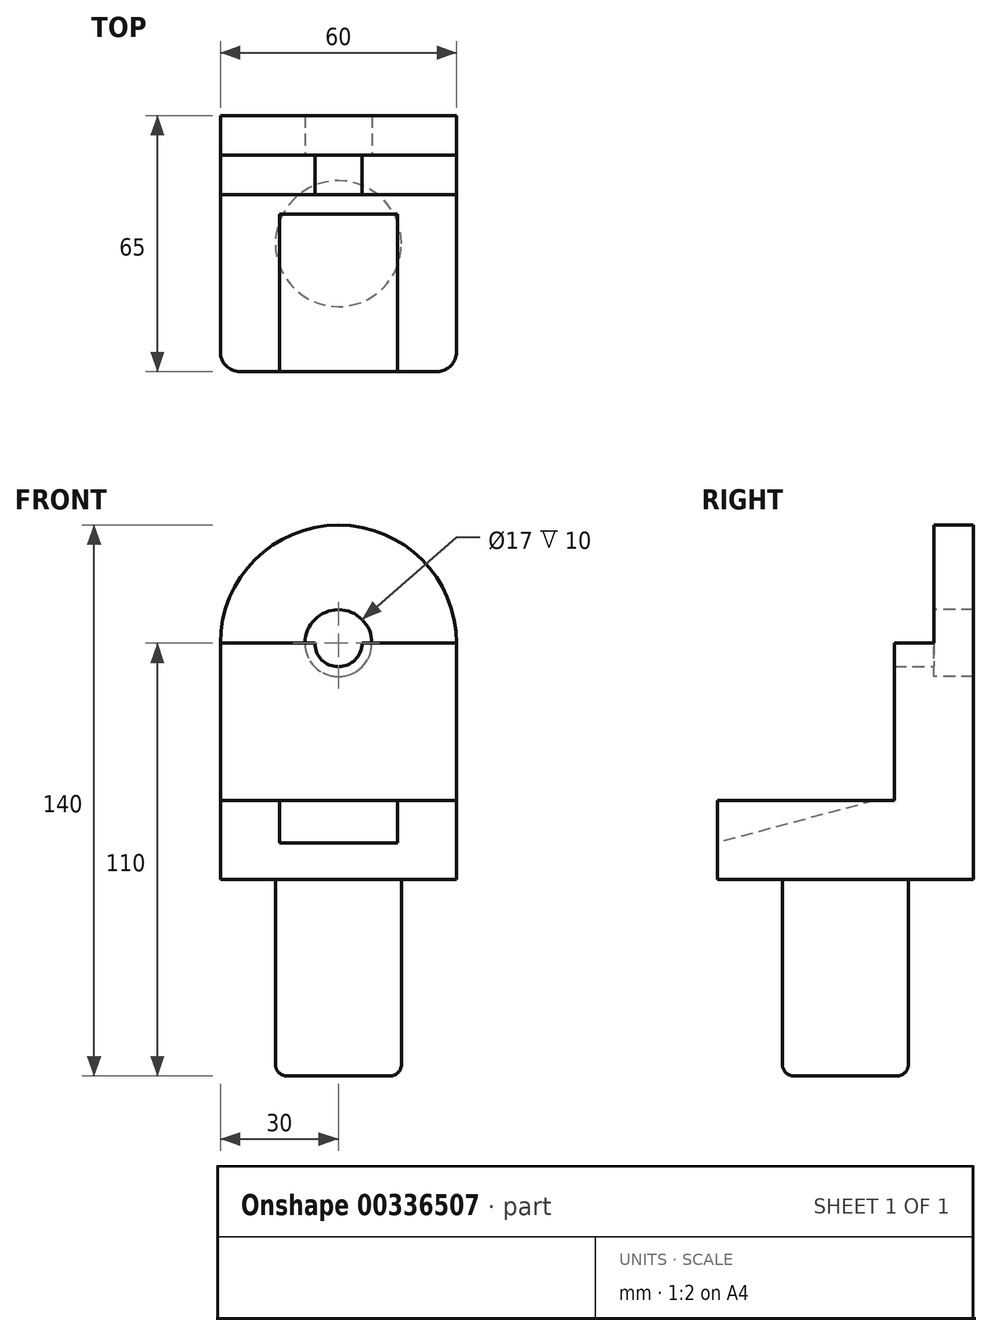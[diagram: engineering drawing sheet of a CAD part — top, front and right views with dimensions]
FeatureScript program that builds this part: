
annotation { "Feature Type Name" : "Feature", "Feature Type Description" : "" }
export const myFeature = defineFeature(function(context is Context, id is Id, definition is map)
    precondition{}
    {
        {
            var Q0;
            Q0=qCreatedBy(makeId("Top.planeOp"),FACE);
            var sketch = newSketch(context, id + "F0", { "sketchPlane" : qUnion([Q0])});
            skCircle(sketch, "E0", {"center": v(0, 0) * mm, "radius": 16 * mm});
            skSolve(sketch);
        }
        {
            var Q0;
            Q0=makeQuery(id+"F0.imprint","IMPRINT",FACE,{"disambiguationData":[TD([[makeQuery(id+"F0.imprint","IMPRINT",EDGE,{"derivedFrom":sQuery(id+"F0.wireOp",EDGE,"E0")}),1.0]])]});
            extrude(context, id + "F1", {"entities" : qUnion([Q0]), "depth" : 50 * mm});
        }
        {
            var Q0;
            Q0=makeQuery(id+"F1.opExtrude","CAP_FACE",FACE,{"disambiguationData":[OSD([sQuery(id+"F0.wireOp",EDGE,"E0")])],"isStart":false});
            var sketch = newSketch(context, id + "F2", { "sketchPlane" : qUnion([Q0])});
            skLineSegment(sketch, "E1", {"start": v(-30, 0) * mm, "end": v(-30, 32.5) * mm});
            skLineSegment(sketch, "E2", {"start": v(0, 32.5) * mm, "end": v(-30, 32.5) * mm});
            skLineSegment(sketch, "E3", {"start": v(30, 0) * mm, "end": v(30, -32.5) * mm});
            skLineSegment(sketch, "E4", {"start": v(0, -32.5) * mm, "end": v(30, -32.5) * mm});
            skLineSegment(sketch, "E5", {"start": v(0, -32.5) * mm, "end": v(-30, -32.5) * mm});
            skLineSegment(sketch, "E6", {"start": v(-30, -32.5) * mm, "end": v(-30, 0) * mm});
            skLineSegment(sketch, "E7", {"start": v(30, 0) * mm, "end": v(30, 32.5) * mm});
            skLineSegment(sketch, "E8", {"start": v(30, 32.5) * mm, "end": v(0, 32.5) * mm});
            skPoint(sketch, "E9.start.orphan", {"position": v(0, 0) * mm});
            skLineSegment(sketch, "E10", {"start": v(-30, 32.5) * mm, "end": v(-30, 7.5) * mm});
            skLineSegment(sketch, "E11", {"start": v(-30, 7.5) * mm, "end": v(30, 7.5) * mm});
            skLineSegment(sketch, "E12", {"start": v(30, -32.5) * mm, "end": v(15, -32.5) * mm});
            skLineSegment(sketch, "E13", {"start": v(30, 7.5) * mm, "end": v(15, 7.5) * mm});
            skLineSegment(sketch, "E14", {"start": v(15, 7.5) * mm, "end": v(15, -32.5) * mm});
            skSolve(sketch);
        }
        {
            var Q0;
            Q0=makeQuery(id+"F2.imprint","IMPRINT",FACE,{"disambiguationData":[TD([[makeQuery(id+"F2.imprint","IMPRINT",EDGE,{"derivedFrom":sQuery(id+"F2.wireOp",EDGE,"E2")}),1.0]])]});
            var Q1;
            {var subQ0=sQuery(id+"F2.wireOp",EDGE,"E11");var subQ1=makeQuery(id+"F1.opExtrude","CAP_EDGE",EDGE,{"disambiguationData":[OSD([sQuery(id+"F0.wireOp",EDGE,"E0")])],"isStart":false});var subQ2=makeQuery(id+"F2.imprint","INTERSECT",VERTEX,{"disambiguationData":[OD(0.0)],"derivedFrom":[subQ1,subQ0]});Q1=makeQuery(id+"F2.imprint","IMPRINT",FACE,{"disambiguationData":[TD([[makeQuery(id+"F2.imprint","IMPRINT",EDGE,{"disambiguationData":[TD([[subQ2,-1.0]])],"derivedFrom":subQ0}),1.0]])]});}
            extrude(context, id + "F3", {"entities" : qUnion([Q0, Q1]), "operationType" : NewBodyOperationType.ADD, "depth" : 20 * mm});
        }
        {
            var Q0;
            {var subQ0=sQuery(id+"F2.wireOp",EDGE,"E14");var subQ1=makeQuery(id+"F1.opExtrude","CAP_EDGE",EDGE,{"disambiguationData":[OSD([sQuery(id+"F0.wireOp",EDGE,"E0")])],"isStart":false});var subQ2=makeQuery(id+"F2.imprint","INTERSECT",VERTEX,{"disambiguationData":[OD(0.0)],"derivedFrom":[subQ1,subQ0]});Q0=makeQuery(id+"F2.imprint","IMPRINT",FACE,{"disambiguationData":[TD([[makeQuery(id+"F2.imprint","IMPRINT",EDGE,{"disambiguationData":[TD([[subQ2,-1.0]])],"derivedFrom":subQ0}),1.0]])]});}
            var Q1;
            {var subQ2=sQuery(id+"F2.wireOp",EDGE,"E3");Q1=makeQuery(id+"F2.imprint","IMPRINT",FACE,{"disambiguationData":[TD([[makeQuery(id+"F2.imprint","IMPRINT",EDGE,{"derivedFrom":subQ2}),-1.0]])]});}
            extrude(context, id + "F4", {"entities" : qUnion([Q0, Q1]), "operationType" : NewBodyOperationType.ADD, "depth" : 20 * mm});
        }
        {
            var Q0;
            Q0=makeQuery(id+"F4.opExtrude","SWEPT_FACE",FACE,{"disambiguationData":[OSD([sQuery(id+"F2.wireOp",EDGE,"E14")])]});
            var sketch = newSketch(context, id + "F5", { "sketchPlane" : qUnion([Q0])});
            skLineSegment(sketch, "E15", {"start": v(-7.5, 70) * mm, "end": v(15.18, 63.92) * mm});
            skLineSegment(sketch, "E16", {"start": v(15.18, 63.92) * mm, "end": v(3.84, 66.96) * mm});
            skLineSegment(sketch, "E17", {"start": v(3.84, 66.96) * mm, "end": v(32.5, 59.28) * mm});
            skSolve(sketch);
        }
        {
            var Q0;
            {var subQ8=sQuery(id+"F5.wireOp",EDGE,"E15");Q0=makeQuery(id+"F5.imprint","IMPRINT",FACE,{"disambiguationData":[TD([[makeQuery(id+"F5.imprint","IMPRINT",EDGE,{"derivedFrom":subQ8}),-1.0]])]});}
            extrude(context, id + "F6", {"entities" : qUnion([Q0]), "operationType" : NewBodyOperationType.ADD, "depth" : 30 * mm});
        }
        {
            var Q0;
            Q0=makeQuery(id+"F3.opExtrude","SWEPT_FACE",FACE,{"disambiguationData":[OSD([sQuery(id+"F2.wireOp",EDGE,"E11"),sQuery(id+"F2.wireOp",EDGE,"E13")])]});
            extrude(context, id + "F7", {"entities" : qUnion([Q0]), "operationType" : NewBodyOperationType.ADD, "depth" : 40 * mm});
        }
        {
            var Q0;
            {var subQ0=sQuery(id+"F2.wireOp",EDGE,"E13");var subQ1=sQuery(id+"F2.wireOp",EDGE,"E11");var subQ2=sQuery(id+"F2.wireOp",EDGE,"E7");Q0=makeQuery(id+"F7.boolean.opBoolean","MERGE",FACE,{"derivedFrom":[makeQuery(id+"F4.boolean.opBoolean","MERGE",FACE,{"derivedFrom":[makeQuery(id+"F3.opExtrude","CAP_FACE",FACE,{"disambiguationData":[OSD([sQuery(id+"F2.wireOp",EDGE,"E2"),subQ2,sQuery(id+"F2.wireOp",EDGE,"E8"),sQuery(id+"F2.wireOp",EDGE,"E10"),subQ1,subQ0])],"isStart":false}),makeQuery(id+"F4.opExtrude","CAP_FACE",FACE,{"disambiguationData":[OSD([sQuery(id+"F2.wireOp",EDGE,"E3"),subQ2,sQuery(id+"F2.wireOp",EDGE,"E12"),subQ0,sQuery(id+"F2.wireOp",EDGE,"E14")])],"isStart":false})]}),makeQuery(id+"F7.opExtrude","SWEPT_FACE",FACE,{"disambiguationData":[OSD([subQ1,subQ0]),TDD([makeQuery(id+"F6.boolean.opBoolean","SPLIT",EDGE,{"derivedFrom":makeQuery(id+"F3.opExtrude","CAP_EDGE",EDGE,{"disambiguationData":[OSD([subQ1,subQ0])],"isStart":false})})])]})]});}
            var sketch = newSketch(context, id + "F8", { "sketchPlane" : qUnion([Q0])});
            skLineSegment(sketch, "E18", {"start": v(-30, 32.5) * mm, "end": v(-30, 22.5) * mm});
            skLineSegment(sketch, "E19", {"start": v(-30, 22.5) * mm, "end": v(30, 22.5) * mm});
            skLineSegment(sketch, "E20", {"start": v(30, 22.5) * mm, "end": v(30, 32.5) * mm});
            skLineSegment(sketch, "E21", {"start": v(-30, 32.5) * mm, "end": v(30, 32.5) * mm});
            skSolve(sketch);
        }
        {
            var Q0;
            Q0 = qSketchRegion(id + "F8", true);
            extrude(context, id + "F9", {"entities" : qUnion([Q0]), "operationType" : NewBodyOperationType.ADD, "depth" : 70 * mm});
        }
        {
            var Q0;
            Q0=makeQuery(id+"F9.opExtrude","CAP_EDGE",EDGE,{"disambiguationData":[OSD([sQuery(id+"F8.wireOp",EDGE,"E18")])],"isStart":false});
            var Q1;
            Q1=makeQuery(id+"F9.opExtrude","CAP_EDGE",EDGE,{"disambiguationData":[OSD([sQuery(id+"F8.wireOp",EDGE,"E20")])],"isStart":false});
            fillet(context, id + "F10", {"entities" : qUnion([Q0, Q1]), "radius" : 30 * mm, "tangentPropagation" : true, "allowEdgeOverflow" : false});
        }
        {
            var Q0;
            Q0=makeQuery(id+"F1.opExtrude","CAP_EDGE",EDGE,{"disambiguationData":[OSD([sQuery(id+"F0.wireOp",EDGE,"E0")])],"isStart":true});
            fillet(context, id + "F11", {"entities" : qUnion([Q0]), "radius" : 3 * mm, "tangentPropagation" : true, "allowEdgeOverflow" : false});
        }
        {
            var Q0;
            Q0=makeQuery(id+"F7.opExtrude","CAP_EDGE",EDGE,{"disambiguationData":[OSD([sQuery(id+"F2.wireOp",EDGE,"E1"),sQuery(id+"F2.wireOp",EDGE,"E10"),sQuery(id+"F2.wireOp",EDGE,"E11")])],"isStart":false});
            var Q1;
            Q1=makeQuery(id+"F4.opExtrude","SWEPT_EDGE",EDGE,{"disambiguationData":[OSD([sQuery(id+"F2.wireOp",EDGE,"E3"),sQuery(id+"F2.wireOp",EDGE,"E12")])]});
            fillet(context, id + "F12", {"entities" : qUnion([Q0, Q1]), "radius" : 5 * mm, "tangentPropagation" : true, "allowEdgeOverflow" : false});
        }
        {
            var Q0;
            Q0=makeQuery(id+"F9.opExtrude","SWEPT_FACE",FACE,{"disambiguationData":[OSD([sQuery(id+"F8.wireOp",EDGE,"E19")])]});
            var sketch = newSketch(context, id + "F13", { "sketchPlane" : qUnion([Q0])});
            skLineSegment(sketch, "E22", {"start": v(0, 140) * mm, "end": v(0, 70) * mm});
            skLineSegment(sketch, "E23", {"start": v(-30, 110) * mm, "end": v(30, 110) * mm});
            skCircle(sketch, "E24", {"center": v(0, 110) * mm, "radius": 10 * mm});
            skCircle(sketch, "E25", {"center": v(0, 110) * mm, "radius": 6 * mm});
            skSolve(sketch);
        }
        {
            var Q0;
            Q0=sQuery(id+"F13.wireOp",VERTEX,"E25.center");
            var Q1;
            Q1=makeQuery(id+"F1.opExtrude","SWEPT_BODY",BODY,{"disambiguationData":[OSD([sQuery(id+"F0.wireOp",EDGE,"E0")])]});
            hole(context, id + "F14", {"style" : HoleStyle.SIMPLE, "endStyle" : HoleEndStyle.THROUGH, "holeDiameter" : 17 * mm, "tappedDepth" : 12 * mm, "tapClearance" : 3, "startFromSketch" : true, "locations" : qUnion([Q0]), "scope" : qUnion([Q1])});
        }
        {
            var Q0;
            {var subQ0=sQuery(id+"F13.wireOp",EDGE,"E25");var subQ1=sQuery(id+"F13.wireOp",EDGE,"E22");var subQ2=makeQuery(id+"F13.imprint","INTERSECT",VERTEX,{"disambiguationData":[OD(1.0)],"derivedFrom":[subQ1,subQ0]});Q0=makeQuery(id+"F13.imprint","IMPRINT",FACE,{"disambiguationData":[TD([[makeQuery(id+"F13.imprint","IMPRINT",EDGE,{"disambiguationData":[TD([[subQ2,-1.0]])],"derivedFrom":subQ1}),-1.0]])]});}
            var Q1;
            {var subQ0=sQuery(id+"F13.wireOp",EDGE,"E24");var subQ1=sQuery(id+"F13.wireOp",EDGE,"E22");var subQ2=makeQuery(id+"F13.imprint","INTERSECT",VERTEX,{"disambiguationData":[OD(0.0)],"derivedFrom":[subQ1,subQ0]});Q1=makeQuery(id+"F13.imprint","IMPRINT",FACE,{"disambiguationData":[TD([[makeQuery(id+"F13.imprint","IMPRINT",EDGE,{"disambiguationData":[TD([[subQ2,-1.0]])],"derivedFrom":subQ1}),-1.0]])]});}
            var Q2;
            {var subQ0=sQuery(id+"F13.wireOp",EDGE,"E24");var subQ1=sQuery(id+"F13.wireOp",EDGE,"E22");var subQ2=makeQuery(id+"F13.imprint","INTERSECT",VERTEX,{"disambiguationData":[OD(0.0)],"derivedFrom":[subQ1,subQ0]});Q2=makeQuery(id+"F13.imprint","IMPRINT",FACE,{"disambiguationData":[TD([[makeQuery(id+"F13.imprint","IMPRINT",EDGE,{"disambiguationData":[TD([[subQ2,-1.0]])],"derivedFrom":subQ1}),1.0]])]});}
            var Q3;
            {var subQ0=sQuery(id+"F13.wireOp",EDGE,"E25");var subQ1=sQuery(id+"F13.wireOp",EDGE,"E22");var subQ2=makeQuery(id+"F13.imprint","INTERSECT",VERTEX,{"disambiguationData":[OD(1.0)],"derivedFrom":[subQ1,subQ0]});Q3=makeQuery(id+"F13.imprint","IMPRINT",FACE,{"disambiguationData":[TD([[makeQuery(id+"F13.imprint","IMPRINT",EDGE,{"disambiguationData":[TD([[subQ2,-1.0]])],"derivedFrom":subQ1}),1.0]])]});}
            extrude(context, id + "F15", {"entities" : qUnion([Q0, Q1, Q2, Q3]), "operationType" : NewBodyOperationType.ADD, "depth" : 10 * mm});
        }
    });
